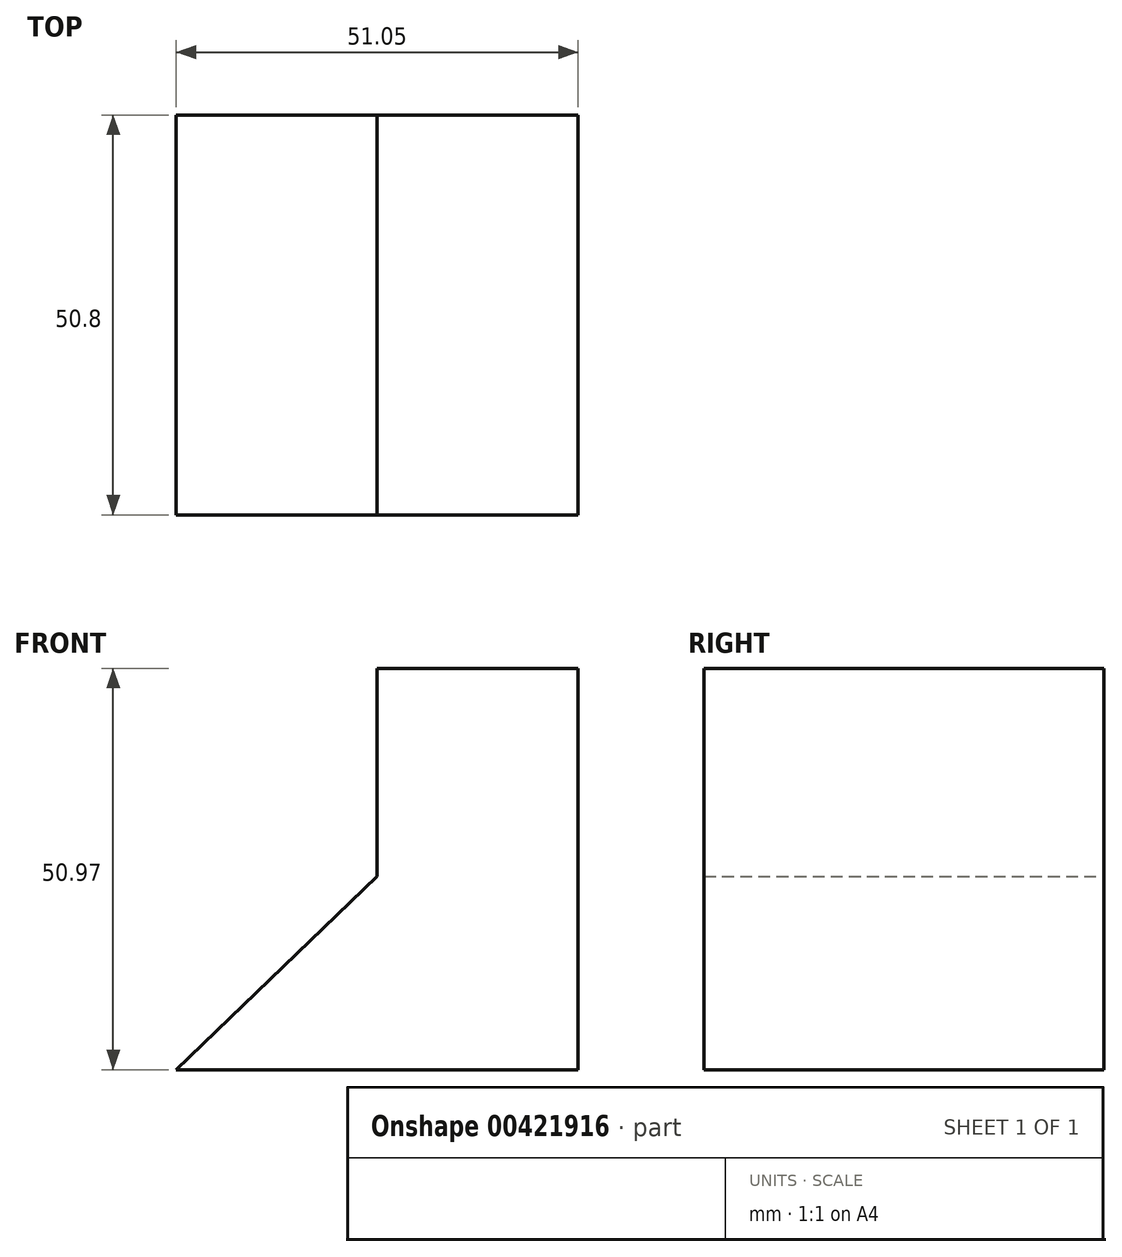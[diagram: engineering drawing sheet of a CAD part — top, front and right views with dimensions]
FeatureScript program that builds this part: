
annotation { "Feature Type Name" : "Feature", "Feature Type Description" : "" }
export const myFeature = defineFeature(function(context is Context, id is Id, definition is map)
    precondition{}
    {
        {
            var Q0;
            Q0=qCreatedBy(makeId("Front.planeOp"),FACE);
            var sketch = newSketch(context, id + "F0", { "sketchPlane" : qUnion([Q0])});
            skLineSegment(sketch, "E0", {"start": v(0, 0) * mm, "end": v(0, 50.97) * mm});
            skLineSegment(sketch, "E1", {"start": v(0, 50.97) * mm, "end": v(-25.53, 50.97) * mm});
            skLineSegment(sketch, "E2", {"start": v(0, 0) * mm, "end": v(-51.05, 0) * mm});
            skLineSegment(sketch, "E3", {"start": v(-25.53, 50.97) * mm, "end": v(-25.53, 24.57) * mm});
            skLineSegment(sketch, "E4", {"start": v(-25.53, 24.57) * mm, "end": v(-51.05, 0) * mm});
            skSolve(sketch);
        }
        {
            var Q0;
            Q0 = qSketchRegion(id + "F0", true);
            extrude(context, id + "F1", {"entities" : qUnion([Q0]), "depth" : 50.8 * mm});
        }
    });
